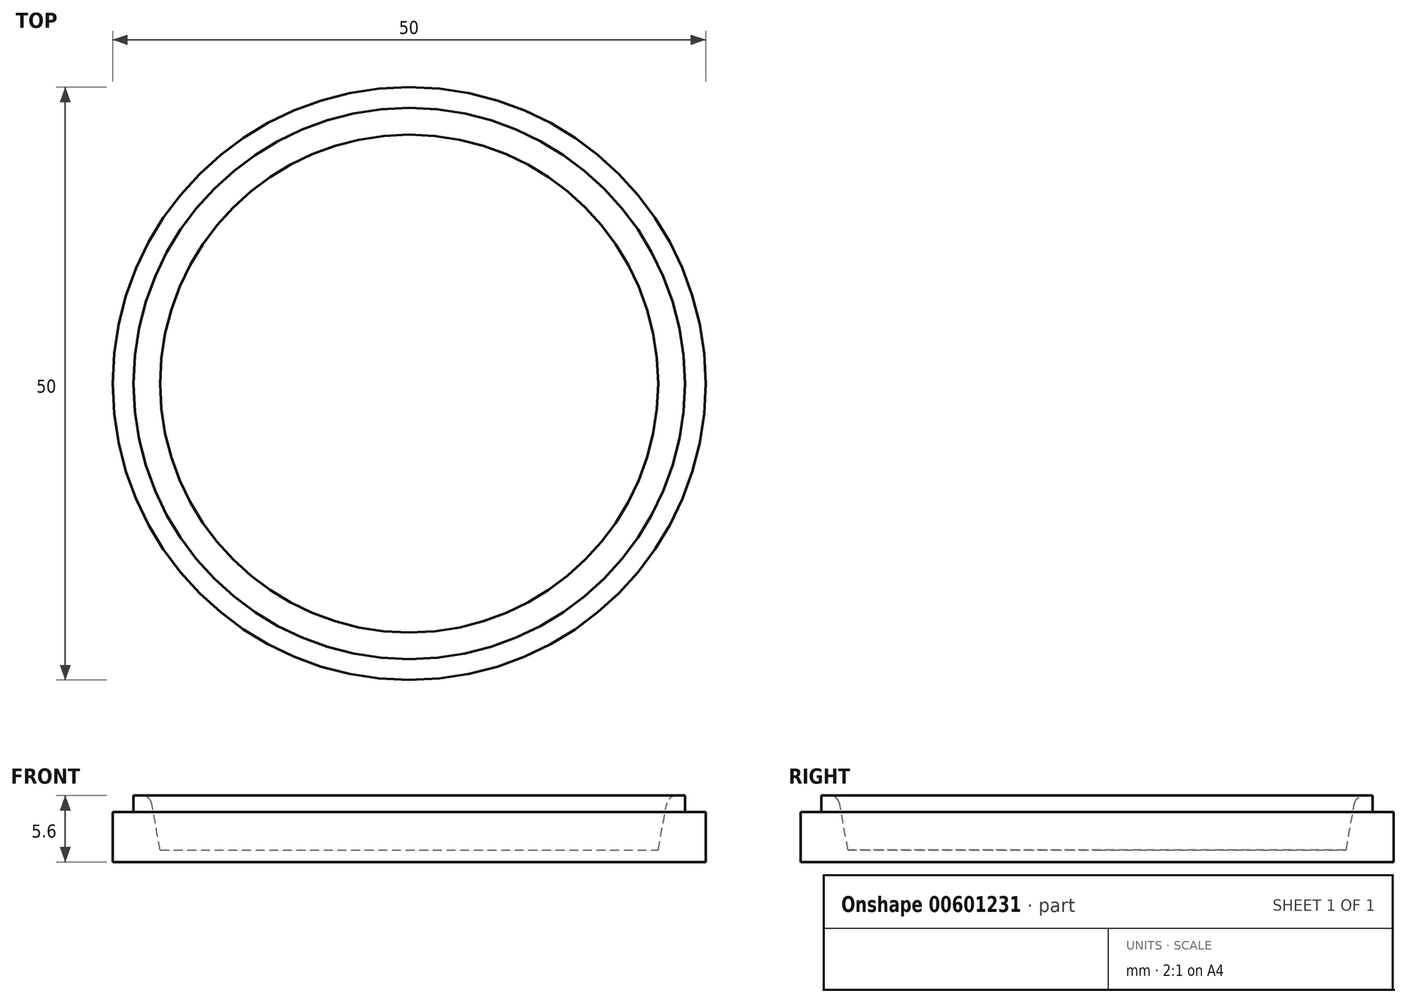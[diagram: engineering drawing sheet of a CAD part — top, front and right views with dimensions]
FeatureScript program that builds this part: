
annotation { "Feature Type Name" : "Feature", "Feature Type Description" : "" }
export const myFeature = defineFeature(function(context is Context, id is Id, definition is map)
    precondition{}
    {
        {
            var Q0;
            Q0=qCreatedBy(makeId("Top.planeOp"),FACE);
            var sketch = newSketch(context, id + "F0", { "sketchPlane" : qUnion([Q0])});
            skCircle(sketch, "E0", {"center": v(0, 0) * mm, "radius": 25 * mm});
            skSolve(sketch);
        }
        {
            var Q0;
            Q0=makeQuery(id+"F0.imprint","IMPRINT",FACE,{"disambiguationData":[TD([[makeQuery(id+"F0.imprint","IMPRINT",EDGE,{"derivedFrom":sQuery(id+"F0.wireOp",EDGE,"E0")}),1.0]])]});
            extrude(context, id + "F1", {"entities" : qUnion([Q0]), "depth" : 1 * mm, "offsetDistance" : 25 * mm});
        }
        {
            var Q0;
            Q0=makeQuery(id+"F1.opExtrude","CAP_FACE",FACE,{"disambiguationData":[OSD([sQuery(id+"F0.wireOp",EDGE,"E0")])],"isStart":false});
            var sketch = newSketch(context, id + "F2", { "sketchPlane" : qUnion([Q0])});
            skCircle(sketch, "E1", {"center": v(0, 0) * mm, "radius": 23.25 * mm});
            skSolve(sketch);
        }
        {
            var Q0;
            Q0=qCreatedBy(makeId("Front.planeOp"),FACE);
            var sketch = newSketch(context, id + "F3", { "sketchPlane" : qUnion([Q0])});
            skLineSegment(sketch, "E2", {"start": v(23.25, 1) * mm, "end": v(23.25, 5.6) * mm});
            skLineSegment(sketch, "E3", {"start": v(23.25, 5.6) * mm, "end": v(21.83, 5.6) * mm});
            skLineSegment(sketch, "E4", {"start": v(21.83, 5.6) * mm, "end": v(21, 1) * mm});
            skLineSegment(sketch, "E5", {"start": v(21, 1) * mm, "end": v(23.25, 1) * mm});
            skSolve(sketch);
        }
        {
            var Q0;
            Q0=makeQuery(id+"F3.imprint","IMPRINT",FACE,{"disambiguationData":[TD([[makeQuery(id+"F3.imprint","IMPRINT",EDGE,{"derivedFrom":sQuery(id+"F3.wireOp",EDGE,"E2")}),1.0]])]});
            var Q1;
            Q1=sQuery(id+"F2.wireOp",EDGE,"E1");
            revolve(context, id + "F4", {"operationType" : NewBodyOperationType.ADD, "surfaceOperationType" : NewSurfaceOperationType.NEW, "entities" : qUnion([Q0]), "axis" : qUnion([Q1]), "revolveType" : RevolveType.FULL});
        }
        {
            var Q0;
            {var subQ0=sQuery(id+"F0.wireOp",EDGE,"E0");Q0=makeQuery(id+"F4.boolean.opBoolean","SPLIT",FACE,{"disambiguationData":[TD([makeQuery(id+"F1.opExtrude","SWEPT_FACE",FACE,{"disambiguationData":[OSD([subQ0])]})])],"derivedFrom":makeQuery(id+"F1.opExtrude","CAP_FACE",FACE,{"disambiguationData":[OSD([subQ0])],"isStart":false})});}
            var sketch = newSketch(context, id + "F5", { "sketchPlane" : qUnion([Q0])});
            skCircle(sketch, "E6", {"center": v(0, 0) * mm, "radius": 23.25 * mm});
            skSolve(sketch);
        }
        {
            var Q0;
            Q0=makeQuery(id+"F5.imprint","IMPRINT",FACE,{"disambiguationData":[TD([[makeQuery(id+"F5.imprint","IMPRINT",EDGE,{"derivedFrom":sQuery(id+"F5.wireOp",EDGE,"E6")}),1.0]])]});
            extrude(context, id + "F6", {"entities" : qUnion([Q0]), "operationType" : NewBodyOperationType.ADD, "depth" : 3.2 * mm, "offsetDistance" : 25 * mm});
        }
        {
            var Q0;
            Q0=makeQuery(id+"F4.opRevolve","SWEPT_EDGE",EDGE,{"disambiguationData":[OSD([sQuery(id+"F3.wireOp",EDGE,"E3"),sQuery(id+"F3.wireOp",EDGE,"E4")])]});
            fillet(context, id + "F7", {"entities" : qUnion([Q0]), "radius" : 0.9 * mm, "tangentPropagation" : true, "allowEdgeOverflow" : false});
        }
    });
